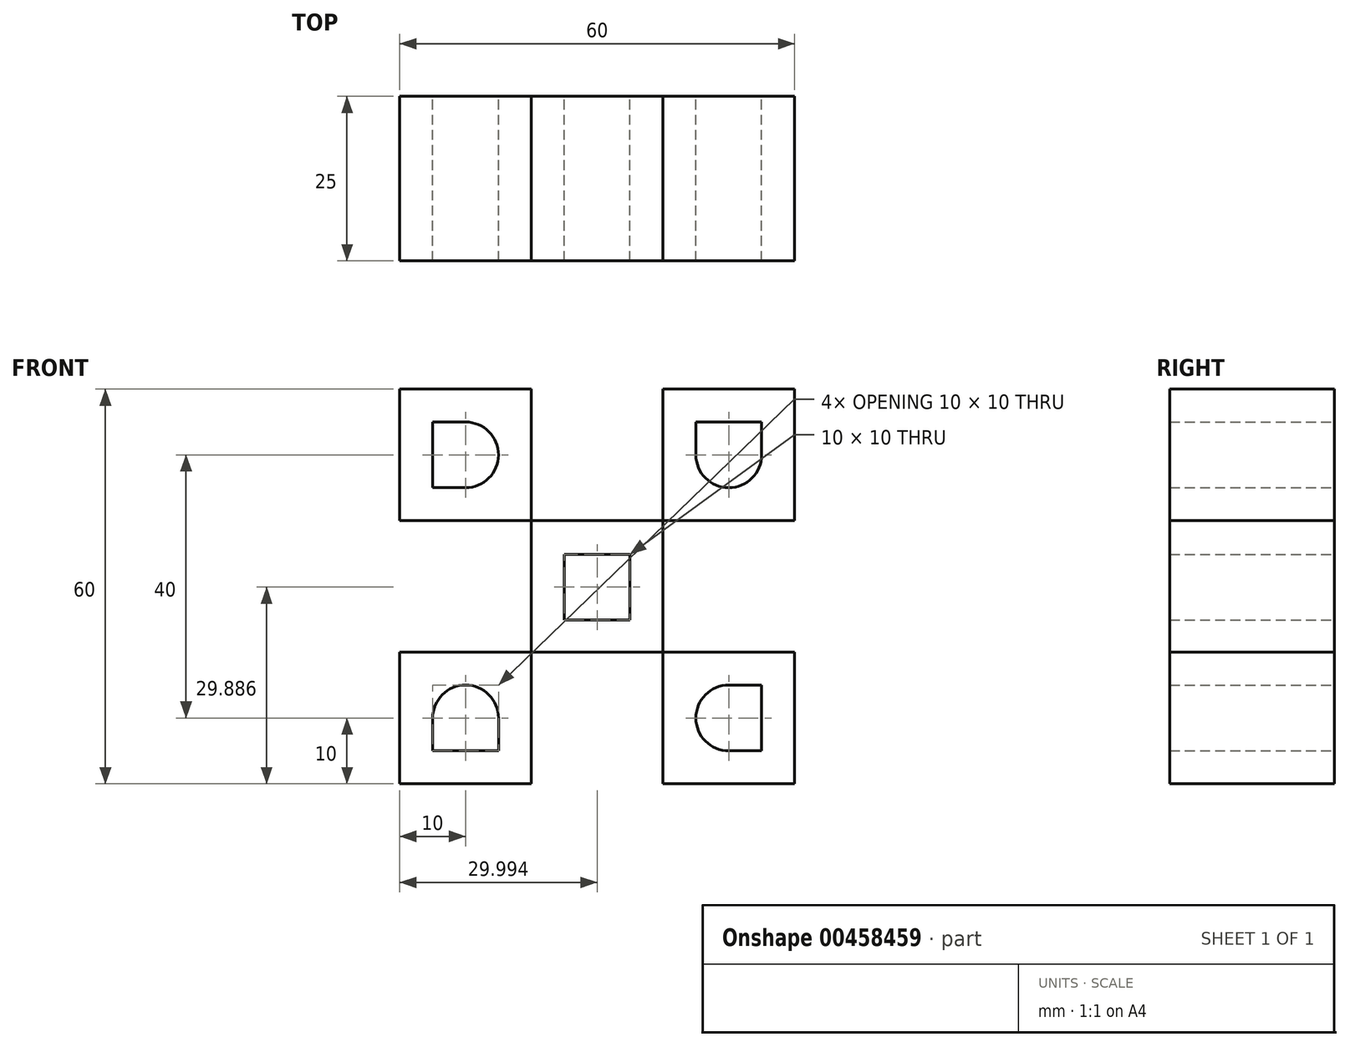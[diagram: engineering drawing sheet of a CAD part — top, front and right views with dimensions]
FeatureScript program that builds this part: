
annotation { "Feature Type Name" : "Feature", "Feature Type Description" : "" }
export const myFeature = defineFeature(function(context is Context, id is Id, definition is map)
    precondition{}
    {
        {
            var Q0;
            Q0=qCreatedBy(makeId("Front.planeOp"),FACE);
            var sketch = newSketch(context, id + "F0", { "sketchPlane" : qUnion([Q0])});
            skLineSegment(sketch, "E0.bottom", {"start": v(0, 0) * mm, "end": v(20, 0) * mm});
            skLineSegment(sketch, "E0.top", {"start": v(0, 20) * mm, "end": v(20, 20) * mm});
            skLineSegment(sketch, "E0.left", {"start": v(0, 0) * mm, "end": v(0, 20) * mm});
            skLineSegment(sketch, "E0.right", {"start": v(20, 0) * mm, "end": v(20, 20) * mm});
            skLineSegment(sketch, "E1.bottom", {"start": v(20, 20) * mm, "end": v(40, 20) * mm});
            skLineSegment(sketch, "E1.top", {"start": v(20, 40) * mm, "end": v(40, 40) * mm});
            skLineSegment(sketch, "E1.left", {"start": v(20, 20) * mm, "end": v(20, 40) * mm});
            skLineSegment(sketch, "E1.right", {"start": v(40, 20) * mm, "end": v(40, 40) * mm});
            skLineSegment(sketch, "E2.bottom", {"start": v(20, 0) * mm, "end": v(40, 0) * mm});
            skLineSegment(sketch, "E2.top", {"start": v(20, -20) * mm, "end": v(40, -20) * mm});
            skLineSegment(sketch, "E2.left", {"start": v(20, 0) * mm, "end": v(20, -20) * mm});
            skLineSegment(sketch, "E2.right", {"start": v(40, 0) * mm, "end": v(40, -20) * mm});
            skLineSegment(sketch, "E3.bottom", {"start": v(0, 0) * mm, "end": v(-20, 0) * mm});
            skLineSegment(sketch, "E3.top", {"start": v(0, -20) * mm, "end": v(-20, -20) * mm});
            skLineSegment(sketch, "E3.left", {"start": v(0, 0) * mm, "end": v(0, -20) * mm});
            skLineSegment(sketch, "E3.right", {"start": v(-20, 0) * mm, "end": v(-20, -20) * mm});
            skLineSegment(sketch, "E4.bottom", {"start": v(0, 20) * mm, "end": v(-20, 20) * mm});
            skLineSegment(sketch, "E4.top", {"start": v(0, 40) * mm, "end": v(-20, 40) * mm});
            skLineSegment(sketch, "E4.left", {"start": v(0, 20) * mm, "end": v(0, 40) * mm});
            skLineSegment(sketch, "E4.right", {"start": v(-20, 20) * mm, "end": v(-20, 40) * mm});
            skLineSegment(sketch, "E5.left", {"start": v(20, 10) * mm, "end": v(20, 30) * mm});
            skLineSegment(sketch, "E5.right", {"start": v(0, 10) * mm, "end": v(0, 30) * mm});
            skPoint(sketch, "E5.middle", {"position": v(10, 20) * mm});
            skLineSegment(sketch, "E6.bottom", {"start": v(15, 14.89) * mm, "end": v(5, 14.89) * mm});
            skLineSegment(sketch, "E6.top", {"start": v(15, 4.89) * mm, "end": v(5, 4.89) * mm});
            skLineSegment(sketch, "E6.left", {"start": v(15, 14.89) * mm, "end": v(15, 4.89) * mm});
            skLineSegment(sketch, "E6.right", {"start": v(5, 14.89) * mm, "end": v(5, 4.89) * mm});
            skPoint(sketch, "E6.middle", {"position": v(10, 9.89) * mm});
            skLineSegment(sketch, "E7.bottom", {"start": v(-15, 35) * mm, "end": v(-10, 35) * mm});
            skLineSegment(sketch, "E7.top", {"start": v(-15, 25) * mm, "end": v(-10, 25) * mm});
            skLineSegment(sketch, "E7.left", {"start": v(-15, 35) * mm, "end": v(-15, 25) * mm});
            skPoint(sketch, "E7.middle", {"position": v(-10, 30) * mm});
            skPoint(sketch, "E8.middle", {"position": v(30, 40) * mm});
            skLineSegment(sketch, "E9.bottom", {"start": v(35, 35) * mm, "end": v(25, 35) * mm});
            skLineSegment(sketch, "E9.left", {"start": v(35, 35) * mm, "end": v(35, 30) * mm});
            skLineSegment(sketch, "E9.right", {"start": v(25, 35) * mm, "end": v(25, 30) * mm});
            skPoint(sketch, "E9.middle", {"position": v(30, 30) * mm});
            skLineSegment(sketch, "E10.left", {"start": v(0, -10) * mm, "end": v(0, 10) * mm});
            skPoint(sketch, "E10.middle", {"position": v(-10, 0) * mm});
            skLineSegment(sketch, "E11.top", {"start": v(-15, -15) * mm, "end": v(-5, -15) * mm});
            skLineSegment(sketch, "E11.left", {"start": v(-15, -10) * mm, "end": v(-15, -15) * mm});
            skLineSegment(sketch, "E11.right", {"start": v(-5, -10) * mm, "end": v(-5, -15) * mm});
            skPoint(sketch, "E11.middle", {"position": v(-10, -10) * mm});
            skLineSegment(sketch, "E12.right", {"start": v(20, -10) * mm, "end": v(20, 10) * mm});
            skPoint(sketch, "E12.middle", {"position": v(30, 0) * mm});
            skLineSegment(sketch, "E13.bottom", {"start": v(30, -5) * mm, "end": v(35, -5) * mm});
            skLineSegment(sketch, "E13.top", {"start": v(30, -15) * mm, "end": v(35, -15) * mm});
            skLineSegment(sketch, "E13.right", {"start": v(35, -5) * mm, "end": v(35, -15) * mm});
            skPoint(sketch, "E13.middle", {"position": v(30, -10) * mm});
            skCircle(sketch, "E14", {"center": v(-10, 30) * mm, "radius": 5 * mm});
            skCircle(sketch, "E15", {"center": v(30, 30) * mm, "radius": 5 * mm});
            skCircle(sketch, "E16", {"center": v(30, -10) * mm, "radius": 5 * mm});
            skPoint(sketch, "E17.orphan", {"position": v(-5, 35) * mm});
            skPoint(sketch, "E18.orphan", {"position": v(-5, 25) * mm});
            skPoint(sketch, "E19.orphan", {"position": v(35, 25) * mm});
            skPoint(sketch, "E9.top.end.orphan", {"position": v(25, 25) * mm});
            skPoint(sketch, "E20.orphan", {"position": v(25, -15) * mm});
            skPoint(sketch, "E13.left.start.orphan", {"position": v(25, -5) * mm});
            skCircle(sketch, "E21", {"center": v(-10, -10) * mm, "radius": 5 * mm});
            skPoint(sketch, "E22.orphan", {"position": v(-15, -5) * mm});
            skPoint(sketch, "E23.orphan", {"position": v(-5, -5) * mm});
            skSolve(sketch);
        }
        {
            var Q0;
            Q0 = qSketchRegion(id + "F0", true);
            extrude(context, id + "F1", {"entities" : qUnion([Q0]), "depth" : 25 * mm});
        }
    });
